# Revit family: Showerhead-American_Standard-Flowise-1660811.002
name_source: partatom
category: Plumbing Fixtures
units: mm (PartAtom-declared; Revit-internal decimal feet)

## family parameters
Always vertical = No
Cut with Voids When Loaded = No
OmniClass Number = 23.45.05.14.17
OmniClass Title = Showers
Part Type = Normal
Room Calculation Point = No
Round Connector Dimension = Use Diameter
Shared = Yes
Work Plane-Based = Yes

## types (1)
- 1660811.002
    1660.240 Standard Shower Arm and Flange = No
    1660.241 Modern Shower Arm and Flange = No
    1660.242 Square Cast Shower Arm = No
    Assembly Code = D2010700
    CEC Compliant = Yes
    CW Connection = No
    CWFU = 3
    CalGreen Compliant = Yes
    Default Elevation = 0"
    Description = Flowise™ Square 1.5 gpm/5.7 L/min Water-Saving Fixed Showerhead
    Finish = Brass-American Standard-002-Polished Chrome
    Flow Rate = 1.5 gpm/5.7 L/min
    HW Connection = No
    HWFU = 3
    Height = 3 3/16"
    IAPMO Compliance = ASME A112.18.1, CSA 125.1
    Manufacturer = American Standard
    Material = Brass-American Standard-002-Polished Chrome
    Model = 1660811.002
    Product Documentation Link = https://americanstandard.box.com
    Product Page URL = https://www.americanstandard-us.com
    Tempered Water Connection = Yes
    Tempered Water Connection Diameter = 1/2"
    URL = https://www.americanstandard-us.com
    Vent Connection = No
    WFU = 4
    Waste Connection = No
    Width = 3 1/4"
    cUPC Compliant = Yes

## geometry (parser evidence)
native form markers: Sweep x2
no freeform markers — native parametric forms only
